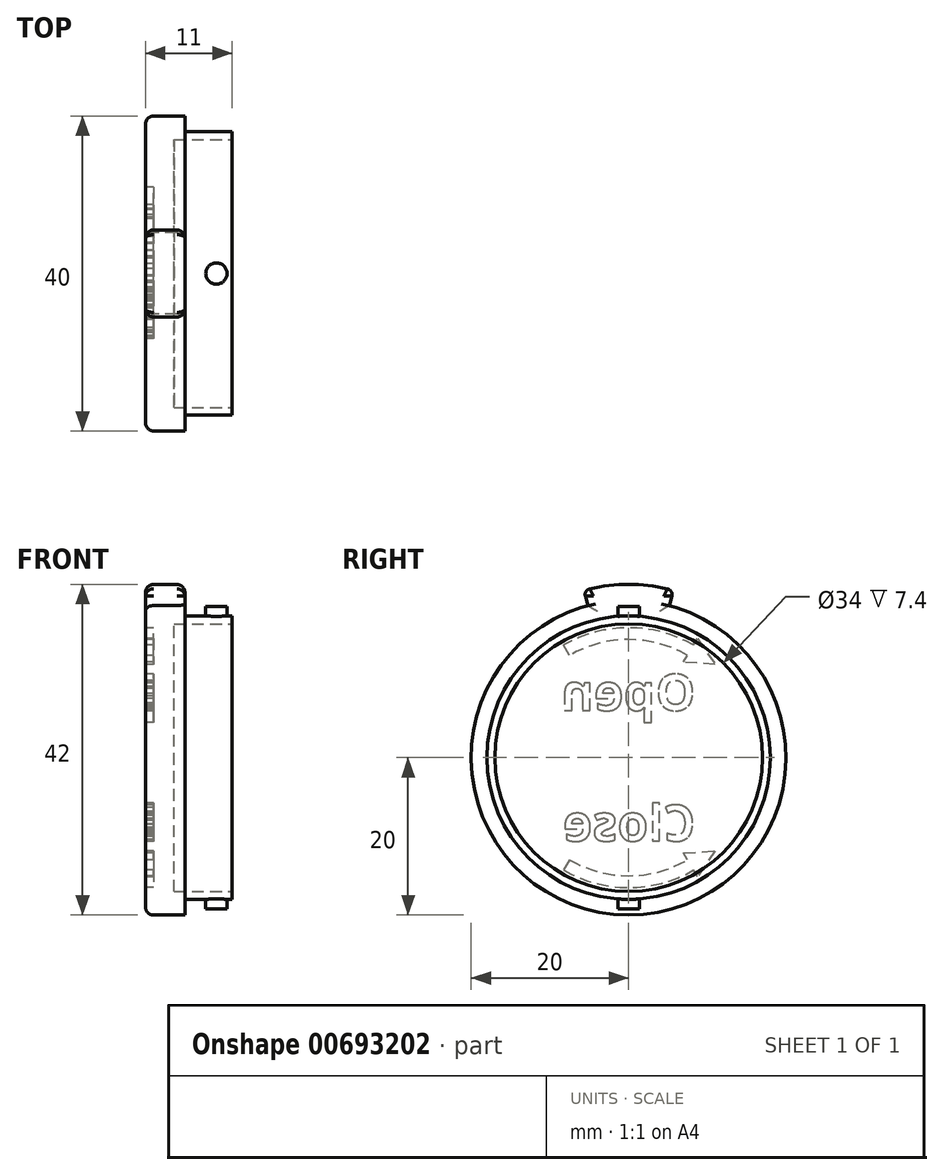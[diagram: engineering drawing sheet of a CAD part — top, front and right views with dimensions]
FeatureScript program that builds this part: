
annotation { "Feature Type Name" : "Feature", "Feature Type Description" : "" }
export const myFeature = defineFeature(function(context is Context, id is Id, definition is map)
    precondition{}
    {
        {
            var Q0;
            Q0=qCreatedBy(makeId("Front.planeOp"),FACE);
            var sketch = newSketch(context, id + "F0", { "sketchPlane" : qUnion([Q0])});
            skLineSegment(sketch, "E0", {"start": v(0, 0) * mm, "end": v(0, 20) * mm});
            skLineSegment(sketch, "E1", {"start": v(0, 20) * mm, "end": v(5, 20) * mm});
            skLineSegment(sketch, "E2", {"start": v(5, 20) * mm, "end": v(5, 18) * mm});
            skLineSegment(sketch, "E3", {"start": v(5, 18) * mm, "end": v(11, 18) * mm});
            skLineSegment(sketch, "E4", {"start": v(11, 18) * mm, "end": v(11, 17) * mm});
            skLineSegment(sketch, "E5", {"start": v(11, 17) * mm, "end": v(3.6, 17) * mm});
            skLineSegment(sketch, "E6", {"start": v(3.6, 17) * mm, "end": v(3.6, 0) * mm});
            skLineSegment(sketch, "E7", {"start": v(3.6, 0) * mm, "end": v(0, 0) * mm});
            skSolve(sketch);
        }
        {
            var Q0;
            Q0 = qSketchRegion(id + "F0", true);
            var Q1;
            Q1=sQuery(id+"F0.wireOp",EDGE,"E6");
            var Q2;
            Q2=sQuery(id+"F0.wireOp",EDGE,"E0");
            var Q3;
            Q3=sQuery(id+"F0.wireOp",EDGE,"E1");
            var Q4;
            Q4=sQuery(id+"F0.wireOp",EDGE,"E2");
            var Q5;
            Q5=sQuery(id+"F0.wireOp",EDGE,"E3");
            var Q6;
            Q6=sQuery(id+"F0.wireOp",EDGE,"E5");
            var Q7;
            Q7=sQuery(id+"F0.wireOp",EDGE,"E4");
            var Q8;
            Q8=sQuery(id+"F0.wireOp",EDGE,"E7");
            revolve(context, id + "F1", {"surfaceOperationType" : NewSurfaceOperationType.ADD, "entities" : qUnion([Q0]), "surfaceEntities" : qUnion([Q1, Q2, Q3, Q4, Q5, Q6, Q7]), "axis" : qUnion([Q8]), "revolveType" : RevolveType.FULL});
        }
        {
            var Q0;
            Q0=qCreatedBy(makeId("Top.planeOp"),FACE);
            var sketch = newSketch(context, id + "F2", { "sketchPlane" : qUnion([Q0])});
            skCircle(sketch, "E8", {"center": v(9, 0) * mm, "radius": 1.35 * mm});
            skSolve(sketch);
        }
        {
            var Q0;
            Q0=makeQuery(id+"F2.imprint","IMPRINT",FACE,{"disambiguationData":[TD([[makeQuery(id+"F2.imprint","IMPRINT",EDGE,{"derivedFrom":sQuery(id+"F2.wireOp",EDGE,"E8")}),1.0]])]});
            extrude(context, id + "F3", {"entities" : qUnion([Q0]), "operationType" : NewBodyOperationType.ADD, "depth" : 19.2 * mm, "offsetDistance" : 25 * mm, "hasSecondDirection" : true, "secondDirectionOppositeDirection" : true, "secondDirectionDepth" : 19.2 * mm});
        }
        {
            var Q0;
            Q0=makeQuery(id+"F1.opRevolve","SWEPT_FACE",FACE,{"disambiguationData":[OSD([sQuery(id+"F0.wireOp",EDGE,"E6")])]});
            extrude(context, id + "F4", {"entities" : qUnion([Q0]), "operationType" : NewBodyOperationType.REMOVE, "endBound" : BoundingType.THROUGH_ALL, "depth" : 25 * mm, "offsetDistance" : 25 * mm});
        }
        {
            var Q0;
            Q0=makeQuery(id+"F1.opRevolve","SWEPT_FACE",FACE,{"disambiguationData":[OSD([sQuery(id+"F0.wireOp",EDGE,"E0")])]});
            var sketch = newSketch(context, id + "F5", { "sketchPlane" : qUnion([Q0])});
            skArc(sketch, "E9", {"start": v(5.7, 21.25) * mm, "mid": v(0, 22) * mm, "end": v(-5.7, 21.25) * mm});
            skArc(sketch, "E10", {"start": v(4.92, 18.35) * mm, "mid": v(0, 19) * mm, "end": v(-4.92, 18.35) * mm});
            skLineSegment(sketch, "E11", {"start": v(-5.7, 21.25) * mm, "end": v(-4.92, 18.35) * mm});
            skLineSegment(sketch, "E12", {"start": v(4.92, 18.35) * mm, "end": v(5.7, 21.25) * mm});
            skSolve(sketch);
        }
        {
            var Q0;
            {var subQ0=sQuery(id+"F5.wireOp",EDGE,"E9");Q0=makeQuery(id+"F5.imprint","IMPRINT",FACE,{"disambiguationData":[TD([[makeQuery(id+"F5.imprint","IMPRINT",EDGE,{"derivedFrom":subQ0}),1.0]])]});}
            var Q1;
            Q1=makeQuery(id+"F1.opRevolve","SWEPT_FACE",FACE,{"disambiguationData":[OSD([sQuery(id+"F0.wireOp",EDGE,"E2")])]});
            extrude(context, id + "F6", {"entities" : qUnion([Q0]), "operationType" : NewBodyOperationType.ADD, "endBound" : BoundingType.UP_TO_SURFACE, "oppositeDirection" : true, "depth" : 25 * mm, "endBoundEntityFace" : qUnion([Q1]), "offsetDistance" : 25 * mm});
        }
        {
            var Q0;
            Q0=makeQuery(id+"F6.opExtrude","SWEPT_EDGE",EDGE,{"disambiguationData":[OSD([sQuery(id+"F0.wireOp",EDGE,"E0"),sQuery(id+"F0.wireOp",EDGE,"E1"),sQuery(id+"F5.wireOp",EDGE,"E12")])]});
            var Q1;
            Q1=makeQuery(id+"F6.opExtrude","SWEPT_EDGE",EDGE,{"disambiguationData":[OSD([sQuery(id+"F5.wireOp",EDGE,"E9"),sQuery(id+"F5.wireOp",EDGE,"E12")])]});
            var Q2;
            Q2=makeQuery(id+"F6.opExtrude","SWEPT_EDGE",EDGE,{"disambiguationData":[OSD([sQuery(id+"F5.wireOp",EDGE,"E9"),sQuery(id+"F5.wireOp",EDGE,"E11")])]});
            var Q3;
            Q3=makeQuery(id+"F6.opExtrude","SWEPT_EDGE",EDGE,{"disambiguationData":[OSD([sQuery(id+"F0.wireOp",EDGE,"E0"),sQuery(id+"F0.wireOp",EDGE,"E1"),sQuery(id+"F5.wireOp",EDGE,"E11")])]});
            fillet(context, id + "F7", {"entities" : qUnion([Q0, Q1, Q2, Q3]), "radius" : 0.75 * mm, "tangentPropagation" : true, "allowEdgeOverflow" : false});
        }
        {
            var Q0;
            {var subQ0=sQuery(id+"F5.wireOp",EDGE,"E12");var subQ1=sQuery(id+"F5.wireOp",EDGE,"E11");var subQ2=sQuery(id+"F5.wireOp",EDGE,"E9");var subQ3=sQuery(id+"F0.wireOp",EDGE,"E1");var subQ4=sQuery(id+"F0.wireOp",EDGE,"E0");Q0=makeQuery(id+"FgVMu1LWXXY3ssf_1.5.F6.boolean.opBoolean","MERGE",FACE,{"derivedFrom":[makeQuery(id+"FgVMu1LWXXY3ssf_1.4.F6.boolean.opBoolean","MERGE",FACE,{"derivedFrom":[makeQuery(id+"FgVMu1LWXXY3ssf_1.3.F6.boolean.opBoolean","MERGE",FACE,{"derivedFrom":[makeQuery(id+"FgVMu1LWXXY3ssf_1.2.F6.boolean.opBoolean","MERGE",FACE,{"derivedFrom":[makeQuery(id+"FgVMu1LWXXY3ssf_1.1.F6.boolean.opBoolean","MERGE",FACE,{"derivedFrom":[makeQuery(id+"FgVMu1LWXXY3ssf_1.-1.F6.boolean.opBoolean","MERGE",FACE,{"derivedFrom":[makeQuery(id+"FgVMu1LWXXY3ssf_1.-2.F6.boolean.opBoolean","MERGE",FACE,{"derivedFrom":[makeQuery(id+"FgVMu1LWXXY3ssf_1.-3.F6.boolean.opBoolean","MERGE",FACE,{"derivedFrom":[makeQuery(id+"FgVMu1LWXXY3ssf_1.-4.F6.boolean.opBoolean","MERGE",FACE,{"derivedFrom":[makeQuery(id+"FgVMu1LWXXY3ssf_1.-5.F6.boolean.opBoolean","MERGE",FACE,{"derivedFrom":[makeQuery(id+"F6.boolean.opBoolean","MERGE",FACE,{"derivedFrom":[makeQuery(id+"F1.opRevolve","SWEPT_FACE",FACE,{"disambiguationData":[OSD([subQ4])]}),makeQuery(id+"F6.opExtrude","CAP_FACE",FACE,{"disambiguationData":[OSD([subQ4,subQ3,subQ2,subQ1,subQ0])],"isStart":true})]}),makeQuery(id+"FgVMu1LWXXY3ssf_1.-5.F6.opExtrude","CAP_FACE",FACE,{"disambiguationData":[OSD([subQ4,subQ3,subQ2,subQ1,subQ0])],"isStart":true})]}),makeQuery(id+"FgVMu1LWXXY3ssf_1.-4.F6.opExtrude","CAP_FACE",FACE,{"disambiguationData":[OSD([subQ4,subQ3,subQ2,subQ1,subQ0])],"isStart":true})]}),makeQuery(id+"FgVMu1LWXXY3ssf_1.-3.F6.opExtrude","CAP_FACE",FACE,{"disambiguationData":[OSD([subQ4,subQ3,subQ2,subQ1,subQ0])],"isStart":true})]}),makeQuery(id+"FgVMu1LWXXY3ssf_1.-2.F6.opExtrude","CAP_FACE",FACE,{"disambiguationData":[OSD([subQ4,subQ3,subQ2,subQ1,subQ0])],"isStart":true})]}),makeQuery(id+"FgVMu1LWXXY3ssf_1.-1.F6.opExtrude","CAP_FACE",FACE,{"disambiguationData":[OSD([subQ4,subQ3,subQ2,subQ1,subQ0])],"isStart":true})]}),makeQuery(id+"FgVMu1LWXXY3ssf_1.1.F6.opExtrude","CAP_FACE",FACE,{"disambiguationData":[OSD([subQ4,subQ3,subQ2,subQ1,subQ0])],"isStart":true})]}),makeQuery(id+"FgVMu1LWXXY3ssf_1.2.F6.opExtrude","CAP_FACE",FACE,{"disambiguationData":[OSD([subQ4,subQ3,subQ2,subQ1,subQ0])],"isStart":true})]}),makeQuery(id+"FgVMu1LWXXY3ssf_1.3.F6.opExtrude","CAP_FACE",FACE,{"disambiguationData":[OSD([subQ4,subQ3,subQ2,subQ1,subQ0])],"isStart":true})]}),makeQuery(id+"FgVMu1LWXXY3ssf_1.4.F6.opExtrude","CAP_FACE",FACE,{"disambiguationData":[OSD([subQ4,subQ3,subQ2,subQ1,subQ0])],"isStart":true})]}),makeQuery(id+"FgVMu1LWXXY3ssf_1.5.F6.opExtrude","CAP_FACE",FACE,{"disambiguationData":[OSD([subQ4,subQ3,subQ2,subQ1,subQ0])],"isStart":true})]});}
            var Q1;
            Q1=makeQuery(id+"F6.opExtrude","CAP_EDGE",EDGE,{"disambiguationData":[OSD([sQuery(id+"F5.wireOp",EDGE,"E9")])],"isStart":false});
            fillet(context, id + "F8", {"entities" : qUnion([Q0, Q1]), "radius" : 1 * mm, "tangentPropagation" : true, "allowEdgeOverflow" : false});
        }
        {
            var Q0;
            {var subQ0=sQuery(id+"F5.wireOp",EDGE,"E10");Q0=makeQuery(id+"F5.imprint","IMPRINT",FACE,{"disambiguationData":[TD([[makeQuery(id+"F5.imprint","IMPRINT",EDGE,{"derivedFrom":subQ0}),1.0]])]});}
            var sketch = newSketch(context, id + "F9", { "sketchPlane" : qUnion([Q0])});
            skText(sketch, "E13", { "text": "Open", "fontName": "OpenSans-Bold.ttf"});
            skText(sketch, "E14", { "text": "Close", "fontName": "OpenSans-Bold.ttf"});
            skArc(sketch, "E15", {"start": v(-8.25, -14.29) * mm, "mid": v(0, -16.5) * mm, "end": v(8.25, -14.29) * mm});
            skLineSegment(sketch, "E16", {"start": v(-8.75, -15.16) * mm, "end": v(-8.25, -14.29) * mm});
            skLineSegment(sketch, "E17", {"start": v(-7, -12.12) * mm, "end": v(-10.99, -11.84) * mm});
            skLineSegment(sketch, "E18", {"start": v(-10.99, -11.84) * mm, "end": v(-8.75, -15.16) * mm});
            skLineSegment(sketch, "E19", {"start": v(-7.5, -13) * mm, "end": v(7.5, 13) * mm, "construction": true});
            skArc(sketch, "E20.trimOffspring", {"start": v(8.25, 14.29) * mm, "mid": v(0, 16.5) * mm, "end": v(-8.25, 14.29) * mm});
            skArc(sketch, "E21.trimOffspring", {"start": v(7.5, 13) * mm, "mid": v(0, 15) * mm, "end": v(-7.5, 13) * mm});
            skLineSegment(sketch, "E22.trimOffspring", {"start": v(7.5, -13) * mm, "end": v(8.25, -14.29) * mm});
            skArc(sketch, "E23.trimOffspring", {"start": v(-7.5, -13) * mm, "mid": v(0, -15) * mm, "end": v(7.5, -13) * mm});
            skLineSegment(sketch, "E24", {"start": v(-7.5, 13) * mm, "end": v(7.5, -13) * mm, "construction": true});
            skLineSegment(sketch, "E25.trimOffspring", {"start": v(-7.5, -13) * mm, "end": v(-7, -12.12) * mm});
            skLineSegment(sketch, "E26", {"start": v(7.5, 13) * mm, "end": v(8.25, 14.29) * mm});
            skLineSegment(sketch, "E27", {"start": v(-8.75, 15.16) * mm, "end": v(-10.99, 11.84) * mm});
            skLineSegment(sketch, "E28", {"start": v(-10.99, 11.84) * mm, "end": v(-7, 12.12) * mm});
            skLineSegment(sketch, "E29", {"start": v(-7, 12.12) * mm, "end": v(-7.5, 13) * mm});
            skLineSegment(sketch, "E30.trimOffspring", {"start": v(-8.25, 14.29) * mm, "end": v(-8.75, 15.16) * mm});
            const initialGuessF9  = {"E13": [-0.0085, 0.006, 1, 0, 0.0046], "E14": [-0.0085, -0.01058, 1, 0, 0.00458]};
            skSetInitialGuess(sketch, initialGuessF9);
            skSolve(sketch);
        }
        {
            var Q0;
            Q0 = qSketchRegion(id + "F9", true);
            extrude(context, id + "F10", {"entities" : qUnion([Q0]), "operationType" : NewBodyOperationType.REMOVE, "oppositeDirection" : true, "depth" : 1 * mm, "offsetDistance" : 25 * mm});
        }
    });
